AUTODESK INVENTOR PART (.ipt)
format: ipt  version: 2013 (Build 170138000, 138)  size: 109,056 bytes
history: native  units: in
note: dims shown in document units (in); Inventor stores cm internally (conversion verified against a paired STEP export)
features: extrude x2, sketch x1
ambient origin geometry x8: Origin, YZ Plane, XZ Plane, XY Plane, X Axis, Y Axis, Z Axis, Center Point
bodies: Solid1 (feature_tree)
feature tree (3):
  extrude  "Extrusion1"  Depth=1.5in
  extrude  "Extrusion2"  Depth=0.125in
  sketch  "Sketch2"  dims[d0=1.5in d1=1.5in d2=0.125in d3=0.6875in d4=1.125in d6=1.0in d7=0.0in d8=0.266in d11=1.0in d12=0.0in d13=0.375in d14=0.266in d15=0.375in]
